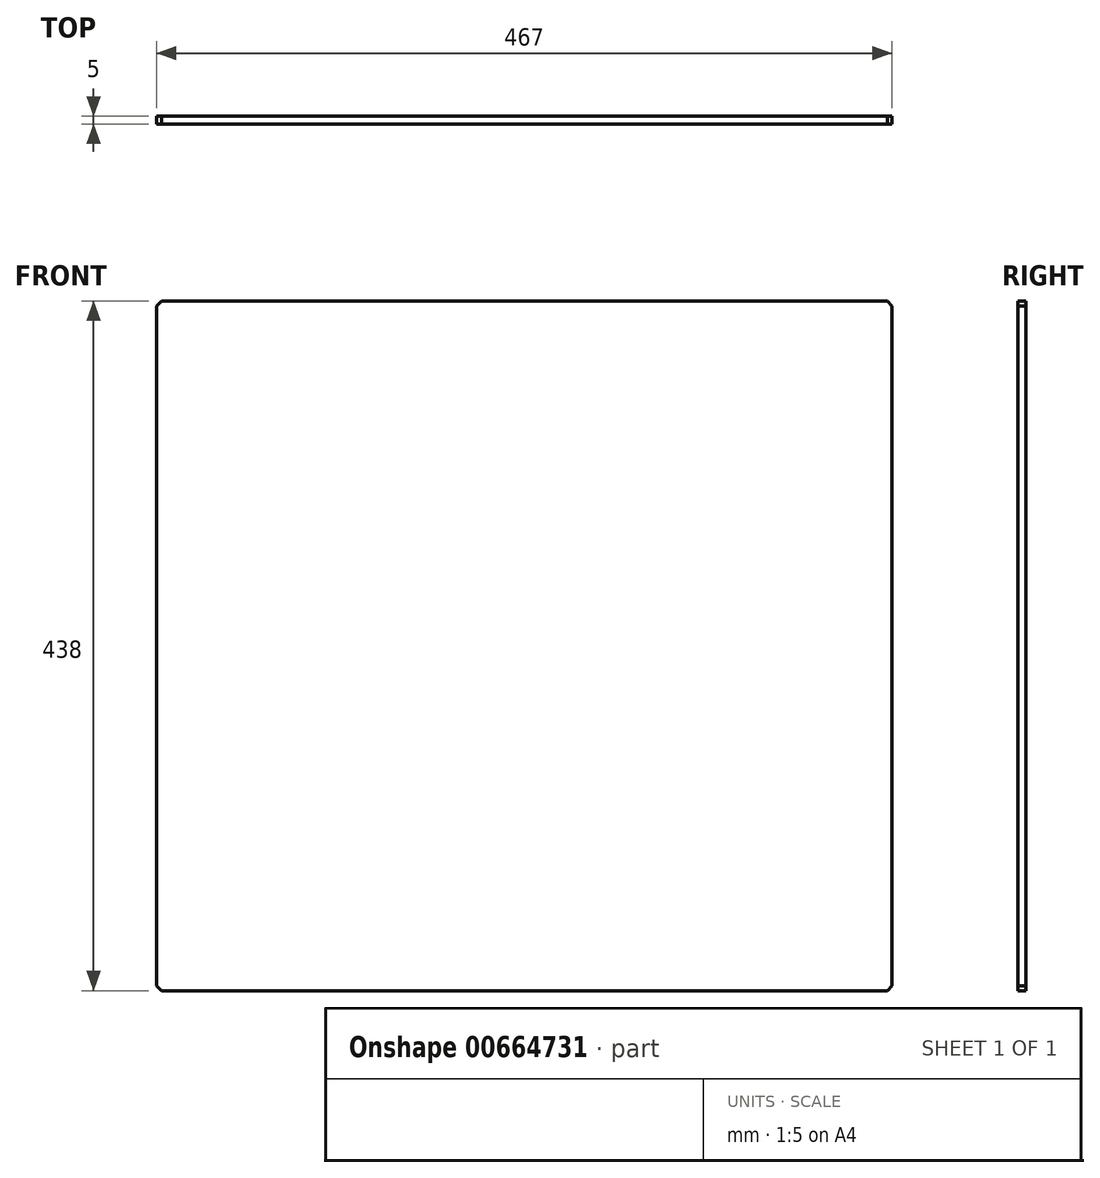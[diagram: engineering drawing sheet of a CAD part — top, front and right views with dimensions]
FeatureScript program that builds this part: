
annotation { "Feature Type Name" : "Feature", "Feature Type Description" : "" }
export const myFeature = defineFeature(function(context is Context, id is Id, definition is map)
    precondition{}
    {
        {
            var Q0;
            Q0=qCreatedBy(makeId("Front.planeOp"),FACE);
            var sketch = newSketch(context, id + "F0", { "sketchPlane" : qUnion([Q0])});
            skLineSegment(sketch, "E0.bottom", {"start": v(-233.5, 219) * mm, "end": v(233.5, 219) * mm});
            skLineSegment(sketch, "E0.top", {"start": v(-233.5, -219) * mm, "end": v(233.5, -219) * mm});
            skLineSegment(sketch, "E0.left", {"start": v(-233.5, 219) * mm, "end": v(-233.5, -219) * mm});
            skLineSegment(sketch, "E0.right", {"start": v(233.5, 219) * mm, "end": v(233.5, -219) * mm});
            skPoint(sketch, "E0.middle", {"position": v(0, 0) * mm});
            skSolve(sketch);
        }
        {
            var Q0;
            Q0=makeQuery(id+"F0.imprint","IMPRINT",FACE,{"disambiguationData":[TD([[makeQuery(id+"F0.imprint","IMPRINT",EDGE,{"derivedFrom":sQuery(id+"F0.wireOp",EDGE,"E0.bottom")}),-1.0]])]});
            extrude(context, id + "F1", {"entities" : qUnion([Q0]), "depth" : 5 * mm, "offsetDistance" : 25 * mm});
        }
        {
            var Q0;
            Q0=makeQuery(id+"F1.opExtrude","SWEPT_EDGE",EDGE,{"disambiguationData":[OSD([sQuery(id+"F0.wireOp",EDGE,"E0.bottom"),sQuery(id+"F0.wireOp",EDGE,"E0.left")])]});
            var Q1;
            Q1=makeQuery(id+"F1.opExtrude","SWEPT_EDGE",EDGE,{"disambiguationData":[OSD([sQuery(id+"F0.wireOp",EDGE,"E0.top"),sQuery(id+"F0.wireOp",EDGE,"E0.left")])]});
            var Q2;
            Q2=makeQuery(id+"F1.opExtrude","SWEPT_EDGE",EDGE,{"disambiguationData":[OSD([sQuery(id+"F0.wireOp",EDGE,"E0.top"),sQuery(id+"F0.wireOp",EDGE,"E0.right")])]});
            var Q3;
            Q3=makeQuery(id+"F1.opExtrude","SWEPT_EDGE",EDGE,{"disambiguationData":[OSD([sQuery(id+"F0.wireOp",EDGE,"E0.bottom"),sQuery(id+"F0.wireOp",EDGE,"E0.right")])]});
            chamfer(context, id + "F2", {"entities" : qUnion([Q0, Q1, Q2, Q3]), "chamferType" : ChamferType.OFFSET_ANGLE, "width" : 3 * mm, "oppositeDirection" : false, "angle" : 45 * degree, "tangentPropagation" : true});
        }
    });
